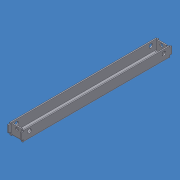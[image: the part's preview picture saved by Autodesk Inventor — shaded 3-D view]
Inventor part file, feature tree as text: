
AUTODESK INVENTOR PART (.ipt)
format: ipt  version: 2015 (Build 190159000, 159)  size: 238,080 bytes
history: native  units: mm
features: sheet_metal_op x9, sketch x8, other x8, plane x1
ambient origin geometry x8: Origin, YZ Plane, XZ Plane, XY Plane, X Axis, Y Axis, Z Axis, Center Point
bodies: Solid1 (feature_tree)
feature tree (26):
  sheet_metal_op  "Face1"
  sheet_metal_op  "Flange1"
  sheet_metal_op  "Flange2"
  plane  "Work Plane1"
  sheet_metal_op  "Flange5"
  sheet_metal_op  "Flange6"
  sketch  "Sketch1"  dims[d2=34.0mm]
  other  "Plate1"
  sketch  "Sketch2"  dims[d3=416.0mm]
  other  "Plate2"
  sheet_metal_op  "Bend1"
  sketch  "Sketch3"  dims[d4=0.001mm]
  other  "Plate3"
  sheet_metal_op  "Bend2"
  sketch  "Sketch7"  dims[d5=-5.0mm d6=-5.0mm]
  sketch  "Sketch8"  dims[d7=0.5mm]
  other  "Plate6"
  sheet_metal_op  "Bend5"
  sketch  "Sketch9"  dims[d8=4.5mm]
  other  "Plate7"
  sheet_metal_op  "Bend6"
  sketch  "Sketch10"  dims[d9=6.0mm]
  sketch  "Sketch11"  dims[d10=0.001mm d11=27.0mm d12=90.0deg d13=0.001mm d14=-5.0mm d15=-5.0mm d16=0.5mm d17=4.5mm d18=6.0mm d19=0.001mm d20=27.0mm d21=90.0deg d22=0.001mm d47=11.0mm d48=11.0mm d49=22.0mm d50=10.0mm d51=22.0mm d52=10.0mm d53=3.0mm d54=0.0mm d55=1.0mm d56=3.0mm d57=3.0mm d58=1.0mm d59=3.0mm d60=3.0mm d61=34.0mm d62=1.0mm d63=0.5mm d64=4.5mm d65=6.0mm d66=0.001mm d67=27.0mm d68=90.0deg d69=0.001mm d70=0.5mm d71=4.5mm d72=6.0mm d73=0.001mm d74=27.0mm d75=90.0deg d76=0.001mm d77=9.0mm d78=13.5mm d79=7.0mm d80=3.0mm d81=0.0mm d82=5.0mm d83=3.0mm d84=5.0mm d85=3.0mm d86=3.0mm d87=0.0mm]
  other  "Cut2"
  other  "Cut3"
  other  "Cut4"
